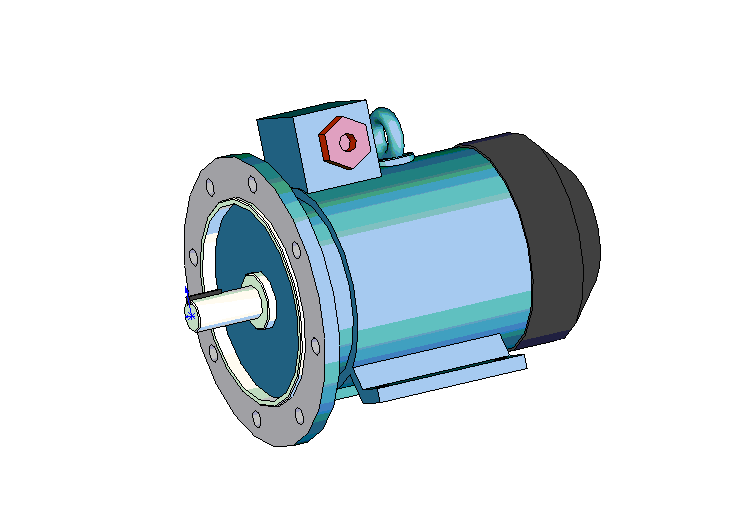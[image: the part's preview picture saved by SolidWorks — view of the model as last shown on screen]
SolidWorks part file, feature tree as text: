
SOLIDWORKS PART (.sldprt)
format: sldprt  version: not decoded by parser v0  size: 701,952 bytes
history: native  units: mm
features: sketch x18, extrude x12, plane x4, cut_extrude x4, chamfer x3, material x1, sweep x1 (+10 scaffold rows collapsed)
feature tree (53):
  scaffold x10  (default folders/planes/origin — collapsed)
  material  "Ст.3 ГОСТ 380-88"
  plane  "Спереди"
  plane  "Сверху"
  plane  "Справа"
  sketch  "Эскиз1"  dims[D1=28.0mm]
  extrude  "Вытянуть1"  Depth=60mm
  sketch  "Эскиз2"  dims[D1=7.0mm D2=7.0mm D3=31.0mm]
  extrude  "Вытянуть2"  Depth=30mm
  sketch  "Эскиз3"  dims[D1=250.0mm]
  extrude  "Вытянуть3"  Depth=14mm
  sketch  "Эскиз4"  dims[D1=180.0mm D2=170.0mm]
  extrude  "Вытянуть4"  Depth=4mm
  sketch  "Эскиз5"  dims[D1=170.0mm D2=50.0mm]
  cut_extrude  "Вырез-Вытянуть1"  Depth=8mm
  chamfer  "Фаска1"  Distance=1mm Angle=45deg
  sketch  "Эскиз6"  dims[c1.D2=15.0mm c1.D1=~135.829276mm c2.D1=22.5deg c2.D3=107.5mm c2.D4=107.5mm c2.D5=107.5mm]
  cut_extrude  "Вырез-Вытянуть2"  [1 undecoded]
  sketch  "Эскиз7"  dims[D1=160.0mm]
  extrude  "Вытянуть5"  Depth=37mm
  sketch  "Эскиз8"  dims[D1=176.0mm]
  extrude  "Вытянуть6"  Depth=166mm
  sketch  "Эскиз9"  dims[D1=180.0mm]
  extrude  "Вытянуть7"  Depth=83mm
  chamfer  "Фаска2"  Distance=35mm Angle=45deg
  sketch  "Эскиз10"  dims[c1.D1=12.0mm c1.D2=94.0mm c1.D3=28.0mm c1.D4=~55.466073mm c2.D4=~177.155724deg c3.D4=10.0mm c3.D5=~54.33349mm c4.D5=30.0deg c4.D6=100.0mm]
  extrude  "Вытянуть8"  Depth=140mm
  sketch  "Эскиз11"  dims[D2=12.0mm D1=123.0mm D3=80.0mm D4=90.0deg D5=160.0mm D6=112.0mm D7=112.0mm D8=235.0mm]
  cut_extrude  "Вырез-Вытянуть3"  [1 undecoded]
  sketch  "Эскиз12"  dims[D1=70.0mm D2=70.0mm D3=1.0mm]
  extrude  "Вытянуть9"  Depth=146.5mm
  sketch  "Эскиз13"  dims[c1.D1=~21.871095mm c1.D2=40.0mm c2.D1=210.0mm]
  extrude  "Вытянуть10"  Depth=92.5mm
  chamfer  "Фаска3"  Distance=1mm Angle=45deg
  plane  "Плоскость1"  Offset=210mm
  sketch  "Эскиз14"  dims[D1=36.0mm]
  sketch  "Эскиз15"  dims[D1=14.0mm D2=36.0mm]
  sweep  "По траектории1"
  sketch  "Эскиз16"  dims[D1=30.0mm D2=30.0mm D3=35.0mm]
  extrude  "Вытянуть11"  Depth=10mm
  sketch  "Эскиз17"  dims[D1=~34.383632mm]
  extrude  "Вытянуть12"  Depth=12mm
  sketch  "Эскиз18"  dims[D1=16.0mm]
  cut_extrude  "Вырез-Вытянуть4"  Depth=12mm
decode coverage: 35 of 38 modeling features carry decoded parameters
note: ~ marks probable driven/reference dimensions
note: 2 parameter values undecoded
note: suppression state not decoded; provenance and decode notes live in map.json
